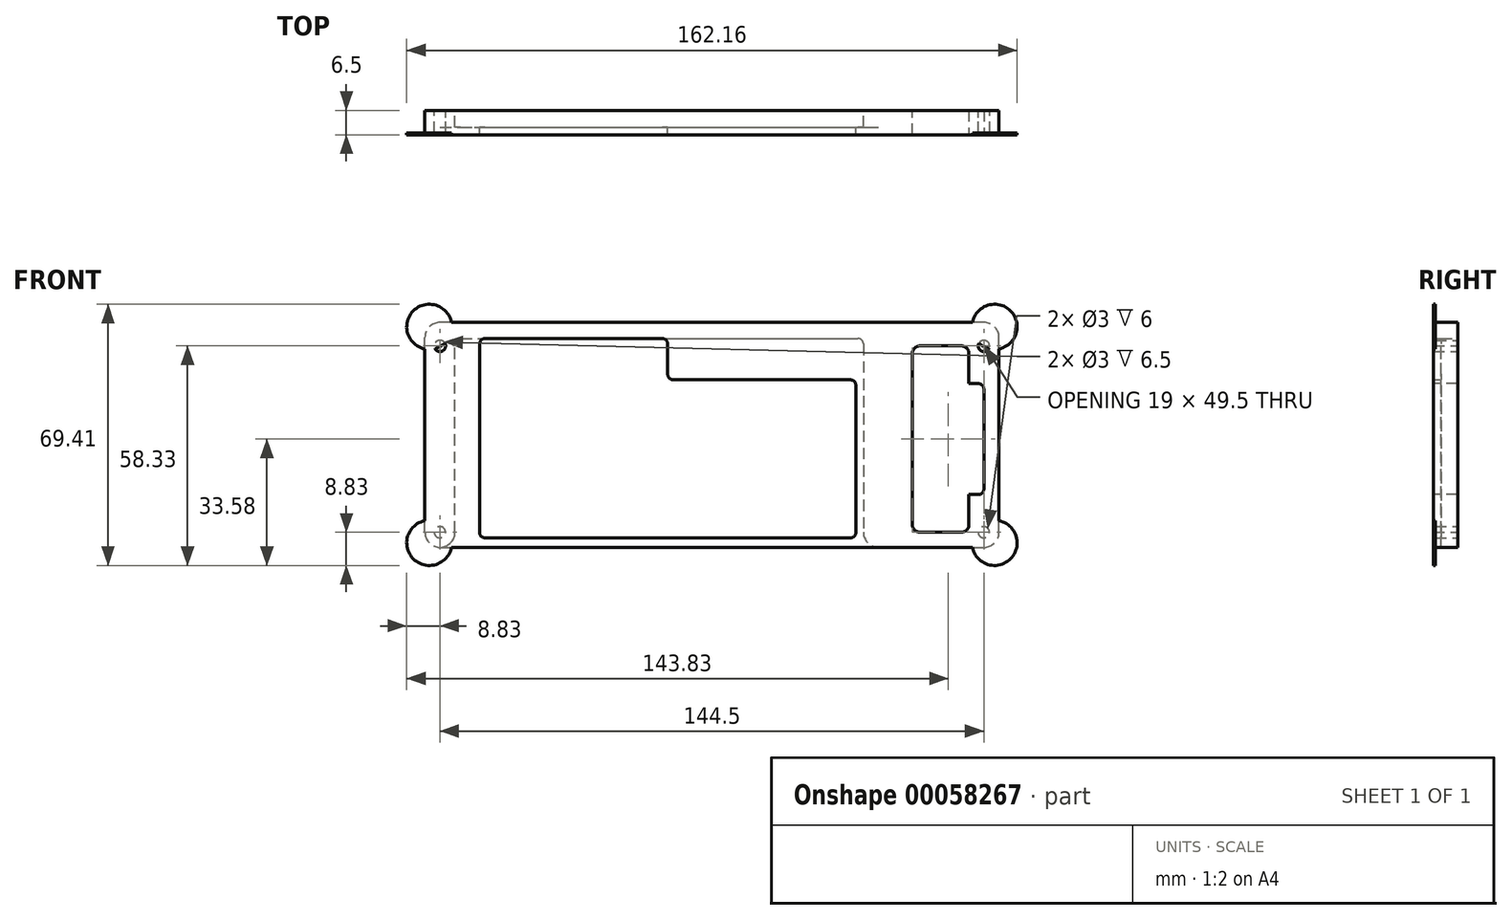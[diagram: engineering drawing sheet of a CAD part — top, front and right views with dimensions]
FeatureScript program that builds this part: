
annotation { "Feature Type Name" : "Feature", "Feature Type Description" : "" }
export const myFeature = defineFeature(function(context is Context, id is Id, definition is map)
    precondition{}
    {
        {
            var Q0;
            Q0=qCreatedBy(makeId("Front.planeOp"),FACE);
            var sketch = newSketch(context, id + "F0", { "sketchPlane" : qUnion([Q0])});
            skLineSegment(sketch, "E0.bottom", {"start": v(72.25, 24.75) * mm, "end": v(-72.25, 24.75) * mm, "construction": true});
            skLineSegment(sketch, "E0.top", {"start": v(72.25, -24.75) * mm, "end": v(-72.25, -24.75) * mm, "construction": true});
            skLineSegment(sketch, "E0.left", {"start": v(72.25, 24.75) * mm, "end": v(72.25, -24.75) * mm, "construction": true});
            skLineSegment(sketch, "E0.right", {"start": v(-72.25, 24.75) * mm, "end": v(-72.25, -24.75) * mm, "construction": true});
            skPoint(sketch, "E0.middle", {"position": v(0, 0) * mm});
            skCircle(sketch, "E1", {"center": v(-72.25, 24.75) * mm, "radius": 1.5 * mm});
            skCircle(sketch, "E2", {"center": v(72.25, 24.75) * mm, "radius": 1.5 * mm});
            skCircle(sketch, "E3", {"center": v(72.25, -24.75) * mm, "radius": 1.5 * mm});
            skCircle(sketch, "E4", {"center": v(-72.25, -24.75) * mm, "radius": 1.5 * mm});
            skLineSegment(sketch, "E5", {"start": v(-68.25, -24.75) * mm, "end": v(-68.25, 24.75) * mm});
            skLineSegment(sketch, "E6", {"start": v(68.25, 24.75) * mm, "end": v(68.25, -24.75) * mm});
            skArc(sketch, "E7", {"start": v(-68.25, -24.75) * mm, "mid": v(-72.25, -28.75) * mm, "end": v(-76.25, -24.75) * mm});
            skLineSegment(sketch, "E8", {"start": v(-76.25, -24.75) * mm, "end": v(-76.25, 27) * mm});
            skLineSegment(sketch, "E9", {"start": v(68.25, -24.75) * mm, "end": v(53.25, -24.75) * mm});
            skLineSegment(sketch, "E10", {"start": v(-68.25, 24.75) * mm, "end": v(40.25, 24.75) * mm, "construction": true});
            skLineSegment(sketch, "E11", {"start": v(40.25, 24.75) * mm, "end": v(40.25, -24.75) * mm});
            skLineSegment(sketch, "E12", {"start": v(53.25, -24.75) * mm, "end": v(53.25, 24.75) * mm});
            skLineSegment(sketch, "E13", {"start": v(53.25, 24.75) * mm, "end": v(68.25, 24.75) * mm});
            skArc(sketch, "E14", {"start": v(76.25, -24.75) * mm, "mid": v(75.08, -27.58) * mm, "end": v(72.25, -28.75) * mm});
            skArc(sketch, "E15", {"start": v(40.25, -24.75) * mm, "mid": v(41.42, -27.58) * mm, "end": v(44.25, -28.75) * mm});
            skLineSegment(sketch, "E16", {"start": v(44.25, -28.75) * mm, "end": v(72.25, -28.75) * mm});
            skLineSegment(sketch, "E17", {"start": v(76.25, -24.75) * mm, "end": v(76.25, 27) * mm});
            skLineSegment(sketch, "E18", {"start": v(72.25, 31) * mm, "end": v(-72.25, 31) * mm});
            skArc(sketch, "E19", {"start": v(76.25, 27) * mm, "mid": v(75.08, 29.83) * mm, "end": v(72.25, 31) * mm});
            skArc(sketch, "E20", {"start": v(-72.25, 31) * mm, "mid": v(-75.08, 29.83) * mm, "end": v(-76.25, 27) * mm});
            skLineSegment(sketch, "E21", {"start": v(-68.25, 24.75) * mm, "end": v(-68.25, 26.75) * mm});
            skLineSegment(sketch, "E22", {"start": v(-68.25, 26.75) * mm, "end": v(40.25, 26.75) * mm});
            skLineSegment(sketch, "E23", {"start": v(40.25, 26.75) * mm, "end": v(40.25, 24.75) * mm});
            skSolve(sketch);
        }
        {
            var Q0;
            Q0 = qSketchRegion(id + "F0", true);
            extrude(context, id + "F1", {"entities" : qUnion([Q0]), "depth" : 4.5 * mm});
        }
        {
            var Q0;
            Q0=makeQuery(id+"F1.opExtrude","SWEPT_EDGE",EDGE,{"disambiguationData":[OSD([sQuery(id+"F0.wireOp",EDGE,"E5"),sQuery(id+"F0.wireOp",EDGE,"E10")])]});
            var Q1;
            Q1=makeQuery(id+"F1.opExtrude","SWEPT_EDGE",EDGE,{"disambiguationData":[OSD([sQuery(id+"F0.wireOp",EDGE,"E10"),sQuery(id+"F0.wireOp",EDGE,"E11")])]});
            var Q2;
            Q2=makeQuery(id+"F1.opExtrude","SWEPT_EDGE",EDGE,{"disambiguationData":[OSD([sQuery(id+"F0.wireOp",EDGE,"E6"),sQuery(id+"F0.wireOp",EDGE,"E13")])]});
            var Q3;
            Q3=makeQuery(id+"F1.opExtrude","SWEPT_EDGE",EDGE,{"disambiguationData":[OSD([sQuery(id+"F0.wireOp",EDGE,"E12"),sQuery(id+"F0.wireOp",EDGE,"E13")])]});
            var Q4;
            Q4=makeQuery(id+"F1.opExtrude","SWEPT_EDGE",EDGE,{"disambiguationData":[OSD([sQuery(id+"F0.wireOp",EDGE,"E9"),sQuery(id+"F0.wireOp",EDGE,"E12")])]});
            var Q5;
            Q5=makeQuery(id+"F1.opExtrude","SWEPT_EDGE",EDGE,{"disambiguationData":[OSD([sQuery(id+"F0.wireOp",EDGE,"E6"),sQuery(id+"F0.wireOp",EDGE,"E9")])]});
            fillet(context, id + "F2", {"entities" : qUnion([Q0, Q1, Q2, Q3, Q4, Q5]), "radius" : 2 * mm, "tangentPropagation" : true, "allowEdgeOverflow" : false});
        }
        {
            var Q0;
            Q0=makeQuery(id+"F1.opExtrude","CAP_FACE",FACE,{"disambiguationData":[OSD([sQuery(id+"F0.wireOp",EDGE,"E1"),sQuery(id+"F0.wireOp",EDGE,"E2"),sQuery(id+"F0.wireOp",EDGE,"E3"),sQuery(id+"F0.wireOp",EDGE,"E4"),sQuery(id+"F0.wireOp",EDGE,"E5"),sQuery(id+"F0.wireOp",EDGE,"E6"),sQuery(id+"F0.wireOp",EDGE,"E7"),sQuery(id+"F0.wireOp",EDGE,"E8"),sQuery(id+"F0.wireOp",EDGE,"E9"),sQuery(id+"F0.wireOp",EDGE,"E10"),sQuery(id+"F0.wireOp",EDGE,"E11"),sQuery(id+"F0.wireOp",EDGE,"E12"),sQuery(id+"F0.wireOp",EDGE,"E13"),sQuery(id+"F0.wireOp",EDGE,"E14"),sQuery(id+"F0.wireOp",EDGE,"E15"),sQuery(id+"F0.wireOp",EDGE,"E16"),sQuery(id+"F0.wireOp",EDGE,"E17"),sQuery(id+"F0.wireOp",EDGE,"E18"),sQuery(id+"F0.wireOp",EDGE,"E19"),sQuery(id+"F0.wireOp",EDGE,"E20")])],"isStart":false});
            var sketch = newSketch(context, id + "F3", { "sketchPlane" : qUnion([Q0])});
            skLineSegment(sketch, "E24.bottom", {"start": v(-61.75, 15.75) * mm, "end": v(-11.75, 15.75) * mm, "construction": true});
            skLineSegment(sketch, "E24.top", {"start": v(-61.75, -26.25) * mm, "end": v(38.25, -26.25) * mm});
            skLineSegment(sketch, "E24.left", {"start": v(-61.75, 15.75) * mm, "end": v(-61.75, -26.25) * mm});
            skLineSegment(sketch, "E24.right", {"start": v(38.25, 15.75) * mm, "end": v(38.25, -26.25) * mm});
            skPoint(sketch, "E25", {"position": v(-72.25, -24.75) * mm});
            skLineSegment(sketch, "E26", {"start": v(-11.75, 15.75) * mm, "end": v(-11.75, 26.75) * mm});
            skLineSegment(sketch, "E27", {"start": v(-11.75, 26.75) * mm, "end": v(-61.75, 26.75) * mm});
            skLineSegment(sketch, "E28", {"start": v(-61.75, 26.75) * mm, "end": v(-61.75, 15.75) * mm});
            skLineSegment(sketch, "E29", {"start": v(-11.75, 15.75) * mm, "end": v(38.25, 15.75) * mm});
            skLineSegment(sketch, "E30.0", {"start": v(-76.25, -24.75) * mm, "end": v(-76.25, 27) * mm});
            skArc(sketch, "E30.1", {"start": v(-72.25, 31) * mm, "mid": v(-75.08, 29.83) * mm, "end": v(-76.25, 27) * mm});
            skCircle(sketch, "E30.2", {"center": v(-72.25, 24.75) * mm, "radius": 1.5 * mm});
            skCircle(sketch, "E30.3", {"center": v(-72.25, -24.75) * mm, "radius": 1.5 * mm});
            skLineSegment(sketch, "E30.4", {"start": v(72.25, 31) * mm, "end": v(-72.25, 31) * mm});
            skCircle(sketch, "E30.5", {"center": v(72.25, 24.75) * mm, "radius": 1.5 * mm});
            skArc(sketch, "E30.6", {"start": v(76.25, 27) * mm, "mid": v(75.08, 29.83) * mm, "end": v(72.25, 31) * mm});
            skLineSegment(sketch, "E30.7", {"start": v(76.25, -24.75) * mm, "end": v(76.25, 27) * mm});
            skArc(sketch, "E30.8", {"start": v(76.25, -24.75) * mm, "mid": v(75.08, -27.58) * mm, "end": v(72.25, -28.75) * mm});
            skCircle(sketch, "E30.9", {"center": v(72.25, -24.75) * mm, "radius": 1.5 * mm});
            skArc(sketch, "E31", {"start": v(-76.25, -24.75) * mm, "mid": v(-75.08, -27.58) * mm, "end": v(-72.25, -28.75) * mm});
            skLineSegment(sketch, "E32", {"start": v(-72.25, -28.75) * mm, "end": v(72.25, -28.75) * mm});
            skLineSegment(sketch, "E33.0", {"start": v(53.25, -22.75) * mm, "end": v(53.25, 22.75) * mm});
            skArc(sketch, "E33.1", {"start": v(53.25, 22.75) * mm, "mid": v(53.84, 24.16) * mm, "end": v(55.25, 24.75) * mm});
            skLineSegment(sketch, "E33.2", {"start": v(55.25, 24.75) * mm, "end": v(66.25, 24.75) * mm});
            skArc(sketch, "E33.3", {"start": v(66.25, 24.75) * mm, "mid": v(67.66, 24.16) * mm, "end": v(68.25, 22.75) * mm});
            skLineSegment(sketch, "E33.4", {"start": v(68.25, 22.75) * mm, "end": v(68.25, -22.75) * mm});
            skArc(sketch, "E33.5", {"start": v(68.25, -22.75) * mm, "mid": v(67.66, -24.16) * mm, "end": v(66.25, -24.75) * mm});
            skLineSegment(sketch, "E33.6", {"start": v(66.25, -24.75) * mm, "end": v(55.25, -24.75) * mm});
            skArc(sketch, "E33.7", {"start": v(55.25, -24.75) * mm, "mid": v(53.84, -24.16) * mm, "end": v(53.25, -22.75) * mm});
            skSolve(sketch);
        }
        {
            var Q0;
            Q0 = qSketchRegion(id + "F3", true);
            extrude(context, id + "F4", {"entities" : qUnion([Q0]), "operationType" : NewBodyOperationType.ADD, "depth" : 2 * mm});
        }
        {
            var Q0;
            Q0=makeQuery(id+"F4.opExtrude","CAP_FACE",FACE,{"disambiguationData":[OSD([sQuery(id+"F3.wireOp",EDGE,"E24.top"),sQuery(id+"F3.wireOp",EDGE,"E24.left"),sQuery(id+"F3.wireOp",EDGE,"E24.right"),sQuery(id+"F3.wireOp",EDGE,"E26"),sQuery(id+"F3.wireOp",EDGE,"E27"),sQuery(id+"F3.wireOp",EDGE,"E28"),sQuery(id+"F3.wireOp",EDGE,"E29"),sQuery(id+"F3.wireOp",EDGE,"E30.0"),sQuery(id+"F3.wireOp",EDGE,"E30.1"),sQuery(id+"F3.wireOp",EDGE,"E30.2"),sQuery(id+"F3.wireOp",EDGE,"E30.3"),sQuery(id+"F3.wireOp",EDGE,"E30.4"),sQuery(id+"F3.wireOp",EDGE,"E30.5"),sQuery(id+"F3.wireOp",EDGE,"E30.6"),sQuery(id+"F3.wireOp",EDGE,"E30.7"),sQuery(id+"F3.wireOp",EDGE,"E30.8"),sQuery(id+"F3.wireOp",EDGE,"E30.9"),sQuery(id+"F3.wireOp",EDGE,"E31"),sQuery(id+"F3.wireOp",EDGE,"E32"),sQuery(id+"F3.wireOp",EDGE,"E33.0"),sQuery(id+"F3.wireOp",EDGE,"E33.1"),sQuery(id+"F3.wireOp",EDGE,"E33.2"),sQuery(id+"F3.wireOp",EDGE,"E33.3"),sQuery(id+"F3.wireOp",EDGE,"E33.4"),sQuery(id+"F3.wireOp",EDGE,"E33.5"),sQuery(id+"F3.wireOp",EDGE,"E33.6"),sQuery(id+"F3.wireOp",EDGE,"E33.7")])],"isStart":false});
            var sketch = newSketch(context, id + "F5", { "sketchPlane" : qUnion([Q0])});
            skLineSegment(sketch, "E34.bottom", {"start": v(68.25, 14.75) * mm, "end": v(72.25, 14.75) * mm});
            skLineSegment(sketch, "E34.top", {"start": v(68.25, -14.75) * mm, "end": v(72.25, -14.75) * mm});
            skLineSegment(sketch, "E34.left", {"start": v(68.25, 14.75) * mm, "end": v(68.25, -14.75) * mm});
            skLineSegment(sketch, "E34.right", {"start": v(72.25, 14.75) * mm, "end": v(72.25, -14.75) * mm});
            skPoint(sketch, "E35", {"position": v(72.25, 24.75) * mm});
            skSolve(sketch);
        }
        {
            var Q0;
            Q0 = qSketchRegion(id + "F5", true);
            extrude(context, id + "F6", {"entities" : qUnion([Q0]), "operationType" : NewBodyOperationType.REMOVE, "endBound" : BoundingType.THROUGH_ALL, "oppositeDirection" : true, "depth" : 25 * mm});
        }
        {
            var Q0;
            Q0=makeQuery(id+"F4.opExtrude","SWEPT_EDGE",EDGE,{"disambiguationData":[OSD([sQuery(id+"F0.wireOp",EDGE,"E10"),sQuery(id+"F3.wireOp",EDGE,"E26"),sQuery(id+"F3.wireOp",EDGE,"E27")])]});
            var Q1;
            Q1=makeQuery(id+"F4.opExtrude","SWEPT_EDGE",EDGE,{"disambiguationData":[OSD([sQuery(id+"F3.wireOp",EDGE,"E26"),sQuery(id+"F3.wireOp",EDGE,"E29")])]});
            var Q2;
            Q2=makeQuery(id+"F4.opExtrude","SWEPT_EDGE",EDGE,{"disambiguationData":[OSD([sQuery(id+"F0.wireOp",EDGE,"E10"),sQuery(id+"F3.wireOp",EDGE,"E27"),sQuery(id+"F3.wireOp",EDGE,"E28")])]});
            var Q3;
            Q3=makeQuery(id+"F4.opExtrude","SWEPT_EDGE",EDGE,{"disambiguationData":[OSD([sQuery(id+"F3.wireOp",EDGE,"E24.right"),sQuery(id+"F3.wireOp",EDGE,"E29")])]});
            var Q4;
            Q4=makeQuery(id+"F4.opExtrude","SWEPT_EDGE",EDGE,{"disambiguationData":[OSD([sQuery(id+"F3.wireOp",EDGE,"E24.top"),sQuery(id+"F3.wireOp",EDGE,"E24.right")])]});
            var Q5;
            Q5=makeQuery(id+"F4.opExtrude","SWEPT_EDGE",EDGE,{"disambiguationData":[OSD([sQuery(id+"F3.wireOp",EDGE,"E24.top"),sQuery(id+"F3.wireOp",EDGE,"E24.left")])]});
            var Q6;
            Q6=makeQuery(id+"F6.boolean.opBoolean","COPY",EDGE,{"derivedFrom":makeQuery(id+"F6.opExtrude","SWEPT_EDGE",EDGE,{"disambiguationData":[OSD([sQuery(id+"F3.wireOp",EDGE,"E33.4"),sQuery(id+"F5.wireOp",EDGE,"E34.bottom"),sQuery(id+"F5.wireOp",EDGE,"E34.left")])]})});
            var Q7;
            Q7=makeQuery(id+"F6.boolean.opBoolean","COPY",EDGE,{"derivedFrom":makeQuery(id+"F6.opExtrude","SWEPT_EDGE",EDGE,{"disambiguationData":[OSD([sQuery(id+"F5.wireOp",EDGE,"E34.bottom"),sQuery(id+"F5.wireOp",EDGE,"E34.right")])]})});
            var Q8;
            Q8=makeQuery(id+"F6.boolean.opBoolean","COPY",EDGE,{"derivedFrom":makeQuery(id+"F6.opExtrude","SWEPT_EDGE",EDGE,{"disambiguationData":[OSD([sQuery(id+"F3.wireOp",EDGE,"E33.4"),sQuery(id+"F5.wireOp",EDGE,"E34.top"),sQuery(id+"F5.wireOp",EDGE,"E34.left")])]})});
            var Q9;
            Q9=makeQuery(id+"F6.boolean.opBoolean","COPY",EDGE,{"derivedFrom":makeQuery(id+"F6.opExtrude","SWEPT_EDGE",EDGE,{"disambiguationData":[OSD([sQuery(id+"F5.wireOp",EDGE,"E34.top"),sQuery(id+"F5.wireOp",EDGE,"E34.right")])]})});
            var Q10;
            Q10=makeQuery(id+"F1.opExtrude","SWEPT_EDGE",EDGE,{"disambiguationData":[OSD([sQuery(id+"F0.wireOp",EDGE,"E22"),sQuery(id+"F0.wireOp",EDGE,"E23")])]});
            var Q11;
            Q11=makeQuery(id+"F1.opExtrude","SWEPT_EDGE",EDGE,{"disambiguationData":[OSD([sQuery(id+"F0.wireOp",EDGE,"E21"),sQuery(id+"F0.wireOp",EDGE,"E22")])]});
            fillet(context, id + "F7", {"entities" : qUnion([Q0, Q1, Q2, Q3, Q4, Q5, Q6, Q7, Q8, Q9, Q10, Q11]), "radius" : 1.5 * mm, "tangentPropagation" : true, "allowEdgeOverflow" : false});
        }
        {
            var Q0;
            Q0=makeQuery(id+"F4.opExtrude","CAP_FACE",FACE,{"disambiguationData":[OSD([sQuery(id+"F3.wireOp",EDGE,"E24.top"),sQuery(id+"F3.wireOp",EDGE,"E24.left"),sQuery(id+"F3.wireOp",EDGE,"E24.right"),sQuery(id+"F3.wireOp",EDGE,"E26"),sQuery(id+"F3.wireOp",EDGE,"E27"),sQuery(id+"F3.wireOp",EDGE,"E28"),sQuery(id+"F3.wireOp",EDGE,"E29"),sQuery(id+"F3.wireOp",EDGE,"E30.0"),sQuery(id+"F3.wireOp",EDGE,"E30.1"),sQuery(id+"F3.wireOp",EDGE,"E30.2"),sQuery(id+"F3.wireOp",EDGE,"E30.3"),sQuery(id+"F3.wireOp",EDGE,"E30.4"),sQuery(id+"F3.wireOp",EDGE,"E30.5"),sQuery(id+"F3.wireOp",EDGE,"E30.6"),sQuery(id+"F3.wireOp",EDGE,"E30.7"),sQuery(id+"F3.wireOp",EDGE,"E30.8"),sQuery(id+"F3.wireOp",EDGE,"E30.9"),sQuery(id+"F3.wireOp",EDGE,"E31"),sQuery(id+"F3.wireOp",EDGE,"E32"),sQuery(id+"F3.wireOp",EDGE,"E33.0"),sQuery(id+"F3.wireOp",EDGE,"E33.1"),sQuery(id+"F3.wireOp",EDGE,"E33.2"),sQuery(id+"F3.wireOp",EDGE,"E33.3"),sQuery(id+"F3.wireOp",EDGE,"E33.4"),sQuery(id+"F3.wireOp",EDGE,"E33.5"),sQuery(id+"F3.wireOp",EDGE,"E33.6"),sQuery(id+"F3.wireOp",EDGE,"E33.7")])],"isStart":false});
            var sketch = newSketch(context, id + "F8", { "sketchPlane" : qUnion([Q0])});
            skCircle(sketch, "E36", {"center": v(-75.08, 29.83) * mm, "radius": 6 * mm});
            skCircle(sketch, "E37", {"center": v(-75.08, -27.58) * mm, "radius": 6 * mm});
            skCircle(sketch, "E38", {"center": v(75.08, 29.83) * mm, "radius": 6 * mm});
            skCircle(sketch, "E39", {"center": v(75.08, -27.58) * mm, "radius": 6 * mm});
            skSolve(sketch);
        }
        {
            var Q0;
            Q0 = qSketchRegion(id + "F8", true);
            extrude(context, id + "F9", {"entities" : qUnion([Q0]), "operationType" : NewBodyOperationType.ADD, "oppositeDirection" : true, "depth" : 0.5 * mm});
        }
    });
